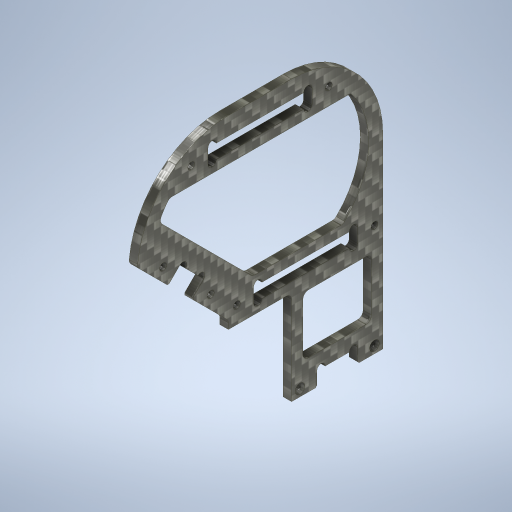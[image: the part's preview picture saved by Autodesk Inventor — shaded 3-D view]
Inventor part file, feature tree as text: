
AUTODESK INVENTOR PART (.ipt)
format: ipt  version: 2024.2 (Build 282272000, 272)  size: 504,832 bytes
history: native  units: mm
features: hole x2, sketch x1, extrude x1, chamfer x1
ambient origin geometry x8: Origin, YZ Plane, XZ Plane, XY Plane, X Axis, Y Axis, Z Axis, Center Point
bodies: Solid1 (feature_tree)
feature tree (5):
  sketch  "Sketch1"  dims[d0=32.5mm d1=9.0mm d2=6.0mm d3=1.5mm d4=5.0mm d5=0.05mm d7=1.5mm d8=70.0mm d10=100.0mm d12=2.0mm d14=2.0mm d15=22.5mm d16=4.0mm d18=2.0mm d19=55.0mm d20=5.0mm d21=5.2mm d22=40.0mm d24=9.0mm d25=6.0mm d26=0.05mm d27=0.05mm d28=6.0mm d29=9.2mm d30=23.0mm d31=17.0mm d32=30.0mm d33=0.05mm d34=5.0mm d35=6.0mm d36=2.5mm d37=4.8mm d38=2.5mm d39=1.0mm d40=50.0mm d41=58.0mm d42=45.0deg d43=30.0mm d44=9.0mm d46=5.0mm d47=6.0mm d48=9.0mm d49=0.05mm d50=0.05mm d52=3.0mm d53=0.0mm d54=5.0mm d56=10.0mm d58=2.0mm d59=5.0mm d61=3.55mm d62=3.5mm d63=4.0mm d64=4.0mm d65=2.0mm d66=90.0deg d67=50.0mm d68=0.0mm d69=2.5mm d70=6.0mm d71=4.0mm d72=2.0mm d73=90.0deg d74=8.0mm d75=0.0mm d76=0.5mm d77=2.0mm d78=45.0deg d79=2.0mm d80=55.0mm d83=2.0mm d84=2.0mm d85=29.321531mm d86=24.5mm d87=2.0mm]
  extrude  "Extrusion1"  Depth=2.0mm
  hole  "Phi3.5"  [1 undecoded]
  hole  "Phi2.5"  [1 undecoded]
  chamfer  "C0.5"  Distance=5.0mm
note: 2 required parameter values undecoded (feature->parameter linkage not recoverable at this tier; creation-order binding heuristic only, values carry confidence <= 0.55)
